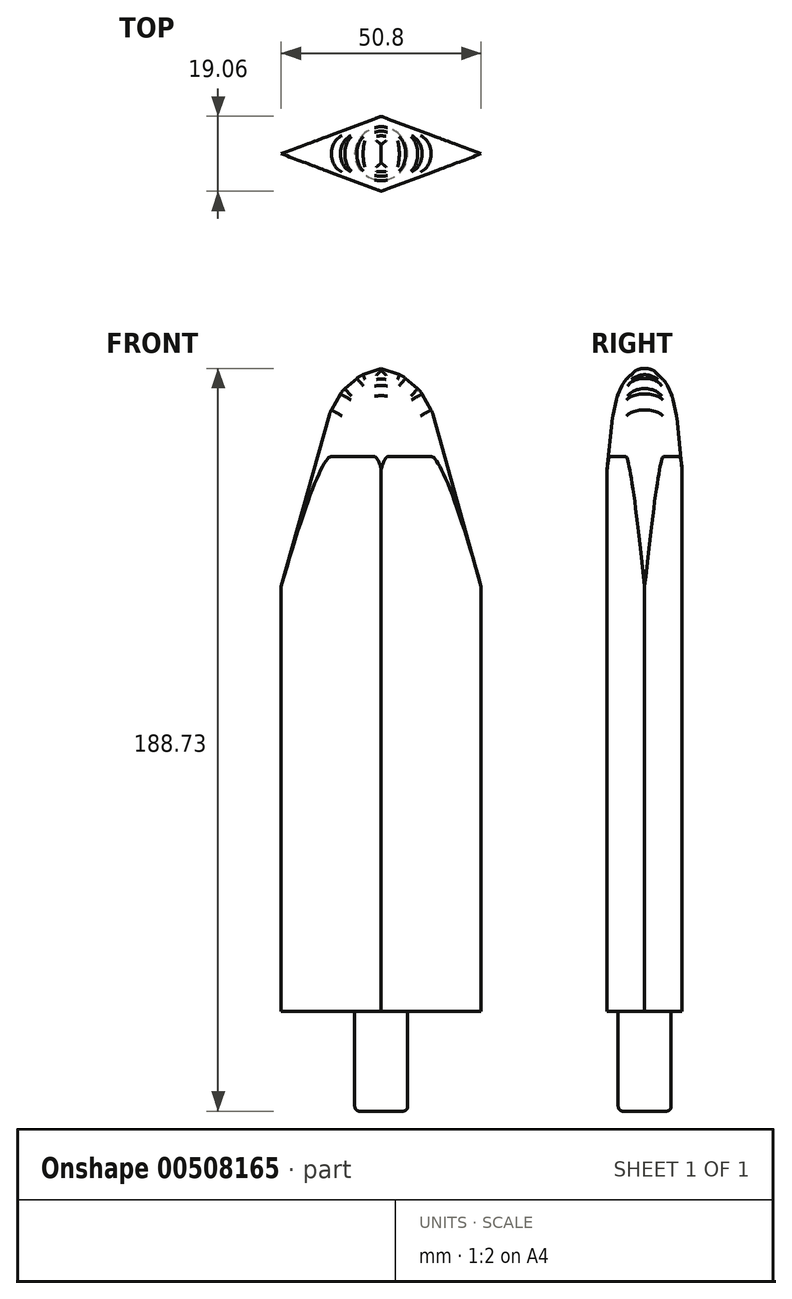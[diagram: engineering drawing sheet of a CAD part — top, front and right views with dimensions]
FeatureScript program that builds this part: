
annotation { "Feature Type Name" : "Feature", "Feature Type Description" : "" }
export const myFeature = defineFeature(function(context is Context, id is Id, definition is map)
    precondition{}
    {
        {
            var Q0;
            Q0=qCreatedBy(makeId("Top.planeOp"),FACE);
            var sketch = newSketch(context, id + "F0", { "sketchPlane" : qUnion([Q0])});
            skLineSegment(sketch, "E0", {"start": v(0, 0) * mm, "end": v(0, 9.53) * mm, "construction": true});
            skLineSegment(sketch, "E1", {"start": v(0, 9.53) * mm, "end": v(0, -9.52) * mm, "construction": true});
            skLineSegment(sketch, "E2", {"start": v(-25.4, 0) * mm, "end": v(25.4, 0) * mm, "construction": true});
            skLineSegment(sketch, "E3", {"start": v(0, 9.53) * mm, "end": v(-25.4, 0) * mm});
            skLineSegment(sketch, "E4", {"start": v(0, 9.53) * mm, "end": v(25.4, 0) * mm});
            skLineSegment(sketch, "E5", {"start": v(25.4, 0) * mm, "end": v(0, -9.52) * mm});
            skLineSegment(sketch, "E6", {"start": v(-25.4, 0) * mm, "end": v(0, -9.52) * mm});
            skSolve(sketch);
        }
        {
            var Q0;
            Q0=qSketchRegion(id+"F0",true);
            extrude(context, id + "F1", {"entities" : qUnion([Q0]), "depth" : 165.1 * mm});
        }
        {
            var Q0;
            Q0=qCreatedBy(makeId("Top.planeOp"),FACE);
            var sketch = newSketch(context, id + "F2", { "sketchPlane" : qUnion([Q0])});
            skCircle(sketch, "E7", {"center": v(0, 0) * mm, "radius": 6.73 * mm});
            skSolve(sketch);
        }
        {
            var Q0;
            Q0=qSketchRegion(id+"F2",true);
            extrude(context, id + "F3", {"entities" : qUnion([Q0]), "operationType" : NewBodyOperationType.ADD, "oppositeDirection" : true, "depth" : 25.4 * mm});
        }
        {
            var Q0;
            Q0=makeQuery(id+"F1.opExtrude","CAP_EDGE",EDGE,{"disambiguationData":[OSD([sQuery(id+"F0.wireOp",EDGE,"E5")])],"isStart":false});
            var Q1;
            Q1=makeQuery(id+"F1.opExtrude","CAP_EDGE",EDGE,{"disambiguationData":[OSD([sQuery(id+"F0.wireOp",EDGE,"E6")])],"isStart":false});
            var Q2;
            Q2=makeQuery(id+"F1.opExtrude","CAP_EDGE",EDGE,{"disambiguationData":[OSD([sQuery(id+"F0.wireOp",EDGE,"E3")])],"isStart":false});
            var Q3;
            Q3=makeQuery(id+"F1.opExtrude","CAP_EDGE",EDGE,{"disambiguationData":[OSD([sQuery(id+"F0.wireOp",EDGE,"E4")])],"isStart":false});
            chamfer(context, id + "F4", {"entities" : qUnion([Q0, Q1, Q2, Q3]), "width" : 8.9 * mm, "tangentPropagation" : true});
        }
        {
            var Q0;
            {var subQ0=sQuery(id+"F0.wireOp",EDGE,"E5");Q0=makeQuery(id+"F4.opChamfer","BLEND_EDGE",EDGE,{"blendedFrom":[makeQuery(id+"F1.opExtrude","CAP_EDGE",EDGE,{"disambiguationData":[OSD([subQ0])],"isStart":false}),makeQuery(id+"F1.opExtrude","SWEPT_FACE",FACE,{"disambiguationData":[OSD([subQ0])]})],"blendedInto":[makeQuery(id+"F1.opExtrude","SWEPT_FACE",FACE,{"disambiguationData":[OSD([subQ0])]})]});}
            var Q1;
            {var subQ0=sQuery(id+"F0.wireOp",EDGE,"E6");Q1=makeQuery(id+"F4.opChamfer","BLEND_EDGE",EDGE,{"blendedFrom":[makeQuery(id+"F1.opExtrude","CAP_EDGE",EDGE,{"disambiguationData":[OSD([subQ0])],"isStart":false}),makeQuery(id+"F1.opExtrude","SWEPT_FACE",FACE,{"disambiguationData":[OSD([subQ0])]})],"blendedInto":[makeQuery(id+"F1.opExtrude","SWEPT_FACE",FACE,{"disambiguationData":[OSD([subQ0])]})]});}
            var Q2;
            {var subQ0=sQuery(id+"F0.wireOp",EDGE,"E4");Q2=makeQuery(id+"F4.opChamfer","BLEND_EDGE",EDGE,{"blendedFrom":[makeQuery(id+"F1.opExtrude","CAP_EDGE",EDGE,{"disambiguationData":[OSD([subQ0])],"isStart":false}),makeQuery(id+"F1.opExtrude","SWEPT_FACE",FACE,{"disambiguationData":[OSD([subQ0])]})],"blendedInto":[makeQuery(id+"F1.opExtrude","SWEPT_FACE",FACE,{"disambiguationData":[OSD([subQ0])]})]});}
            var Q3;
            {var subQ0=sQuery(id+"F0.wireOp",EDGE,"E3");Q3=makeQuery(id+"F4.opChamfer","BLEND_EDGE",EDGE,{"blendedFrom":[makeQuery(id+"F1.opExtrude","CAP_EDGE",EDGE,{"disambiguationData":[OSD([subQ0])],"isStart":false}),makeQuery(id+"F1.opExtrude","SWEPT_FACE",FACE,{"disambiguationData":[OSD([subQ0])]})],"blendedInto":[makeQuery(id+"F1.opExtrude","SWEPT_FACE",FACE,{"disambiguationData":[OSD([subQ0])]})]});}
            chamfer(context, id + "F5", {"entities" : qUnion([Q0, Q1, Q2, Q3]), "width" : 5.08 * mm, "tangentPropagation" : true});
        }
        {
            var Q0;
            {var subQ0=sQuery(id+"F0.wireOp",EDGE,"E4");var subQ1=makeQuery(id+"F1.opExtrude","SWEPT_FACE",FACE,{"disambiguationData":[OSD([subQ0])]});Q0=makeQuery(id+"F5.opChamfer","BLEND_EDGE",EDGE,{"blendedFrom":[makeQuery(id+"F4.opChamfer","BLEND_EDGE",EDGE,{"blendedFrom":[makeQuery(id+"F1.opExtrude","CAP_EDGE",EDGE,{"disambiguationData":[OSD([subQ0])],"isStart":false}),subQ1],"blendedInto":[subQ1]}),subQ1],"blendedInto":[subQ1]});}
            var Q1;
            {var subQ0=sQuery(id+"F0.wireOp",EDGE,"E3");var subQ1=makeQuery(id+"F1.opExtrude","SWEPT_FACE",FACE,{"disambiguationData":[OSD([subQ0])]});Q1=makeQuery(id+"F5.opChamfer","BLEND_EDGE",EDGE,{"blendedFrom":[makeQuery(id+"F4.opChamfer","BLEND_EDGE",EDGE,{"blendedFrom":[makeQuery(id+"F1.opExtrude","CAP_EDGE",EDGE,{"disambiguationData":[OSD([subQ0])],"isStart":false}),subQ1],"blendedInto":[subQ1]}),subQ1],"blendedInto":[subQ1]});}
            var Q2;
            {var subQ0=sQuery(id+"F0.wireOp",EDGE,"E6");var subQ1=makeQuery(id+"F1.opExtrude","SWEPT_FACE",FACE,{"disambiguationData":[OSD([subQ0])]});Q2=makeQuery(id+"F5.opChamfer","BLEND_EDGE",EDGE,{"blendedFrom":[makeQuery(id+"F4.opChamfer","BLEND_EDGE",EDGE,{"blendedFrom":[makeQuery(id+"F1.opExtrude","CAP_EDGE",EDGE,{"disambiguationData":[OSD([subQ0])],"isStart":false}),subQ1],"blendedInto":[subQ1]}),subQ1],"blendedInto":[subQ1]});}
            var Q3;
            {var subQ0=sQuery(id+"F0.wireOp",EDGE,"E5");var subQ1=makeQuery(id+"F1.opExtrude","SWEPT_FACE",FACE,{"disambiguationData":[OSD([subQ0])]});Q3=makeQuery(id+"F5.opChamfer","BLEND_EDGE",EDGE,{"blendedFrom":[makeQuery(id+"F4.opChamfer","BLEND_EDGE",EDGE,{"blendedFrom":[makeQuery(id+"F1.opExtrude","CAP_EDGE",EDGE,{"disambiguationData":[OSD([subQ0])],"isStart":false}),subQ1],"blendedInto":[subQ1]}),subQ1],"blendedInto":[subQ1]});}
            chamfer(context, id + "F6", {"entities" : qUnion([Q0, Q1, Q2, Q3]), "width" : 5.08 * mm, "tangentPropagation" : true});
        }
        {
            var Q0;
            {var subQ0=sQuery(id+"F0.wireOp",EDGE,"E4");var subQ1=makeQuery(id+"F1.opExtrude","SWEPT_FACE",FACE,{"disambiguationData":[OSD([subQ0])]});var subQ2=subQ1;Q0=makeQuery(id+"F6.opChamfer","BLEND_EDGE",EDGE,{"blendedFrom":[makeQuery(id+"F5.opChamfer","BLEND_EDGE",EDGE,{"blendedFrom":[makeQuery(id+"F4.opChamfer","BLEND_EDGE",EDGE,{"blendedFrom":[makeQuery(id+"F1.opExtrude","CAP_EDGE",EDGE,{"disambiguationData":[OSD([subQ0])],"isStart":false}),subQ1],"blendedInto":[subQ1]}),subQ2],"blendedInto":[subQ2]}),subQ2],"blendedInto":[subQ2]});}
            var Q1;
            {var subQ0=sQuery(id+"F0.wireOp",EDGE,"E3");var subQ1=makeQuery(id+"F1.opExtrude","SWEPT_FACE",FACE,{"disambiguationData":[OSD([subQ0])]});var subQ2=subQ1;Q1=makeQuery(id+"F6.opChamfer","BLEND_EDGE",EDGE,{"blendedFrom":[makeQuery(id+"F5.opChamfer","BLEND_EDGE",EDGE,{"blendedFrom":[makeQuery(id+"F4.opChamfer","BLEND_EDGE",EDGE,{"blendedFrom":[makeQuery(id+"F1.opExtrude","CAP_EDGE",EDGE,{"disambiguationData":[OSD([subQ0])],"isStart":false}),subQ1],"blendedInto":[subQ1]}),subQ2],"blendedInto":[subQ2]}),subQ2],"blendedInto":[subQ2]});}
            var Q2;
            {var subQ0=sQuery(id+"F0.wireOp",EDGE,"E6");var subQ1=makeQuery(id+"F1.opExtrude","SWEPT_FACE",FACE,{"disambiguationData":[OSD([subQ0])]});var subQ2=subQ1;Q2=makeQuery(id+"F6.opChamfer","BLEND_EDGE",EDGE,{"blendedFrom":[makeQuery(id+"F5.opChamfer","BLEND_EDGE",EDGE,{"blendedFrom":[makeQuery(id+"F4.opChamfer","BLEND_EDGE",EDGE,{"blendedFrom":[makeQuery(id+"F1.opExtrude","CAP_EDGE",EDGE,{"disambiguationData":[OSD([subQ0])],"isStart":false}),subQ1],"blendedInto":[subQ1]}),subQ2],"blendedInto":[subQ2]}),subQ2],"blendedInto":[subQ2]});}
            var Q3;
            {var subQ0=sQuery(id+"F0.wireOp",EDGE,"E5");var subQ1=makeQuery(id+"F1.opExtrude","SWEPT_FACE",FACE,{"disambiguationData":[OSD([subQ0])]});var subQ2=subQ1;Q3=makeQuery(id+"F6.opChamfer","BLEND_EDGE",EDGE,{"blendedFrom":[makeQuery(id+"F5.opChamfer","BLEND_EDGE",EDGE,{"blendedFrom":[makeQuery(id+"F4.opChamfer","BLEND_EDGE",EDGE,{"blendedFrom":[makeQuery(id+"F1.opExtrude","CAP_EDGE",EDGE,{"disambiguationData":[OSD([subQ0])],"isStart":false}),subQ1],"blendedInto":[subQ1]}),subQ2],"blendedInto":[subQ2]}),subQ2],"blendedInto":[subQ2]});}
            chamfer(context, id + "F7", {"entities" : qUnion([Q0, Q1, Q2, Q3]), "width" : 5.08 * mm, "tangentPropagation" : true});
        }
        {
            var Q0;
            {var subQ0=sQuery(id+"F0.wireOp",EDGE,"E4");var subQ1=makeQuery(id+"F1.opExtrude","SWEPT_FACE",FACE,{"disambiguationData":[OSD([subQ0])]});var subQ2=subQ1;Q0=makeQuery(id+"F7.opChamfer","BLEND_EDGE",EDGE,{"blendedFrom":[makeQuery(id+"F6.opChamfer","BLEND_EDGE",EDGE,{"blendedFrom":[makeQuery(id+"F5.opChamfer","BLEND_EDGE",EDGE,{"blendedFrom":[makeQuery(id+"F4.opChamfer","BLEND_EDGE",EDGE,{"blendedFrom":[makeQuery(id+"F1.opExtrude","CAP_EDGE",EDGE,{"disambiguationData":[OSD([subQ0])],"isStart":false}),subQ1],"blendedInto":[subQ1]}),subQ2],"blendedInto":[subQ2]}),subQ2],"blendedInto":[subQ2]}),makeQuery(id+"F6.opChamfer","BLEND_FACE",FACE,{"disambiguationData":[OSD([subQ0])]})],"blendedInto":[makeQuery(id+"F6.opChamfer","BLEND_FACE",FACE,{"disambiguationData":[OSD([subQ0])]})]});}
            var Q1;
            {var subQ0=sQuery(id+"F0.wireOp",EDGE,"E4");var subQ1=makeQuery(id+"F1.opExtrude","SWEPT_FACE",FACE,{"disambiguationData":[OSD([subQ0])]});Q1=makeQuery(id+"F6.opChamfer","BLEND_EDGE",EDGE,{"blendedFrom":[makeQuery(id+"F5.opChamfer","BLEND_EDGE",EDGE,{"blendedFrom":[makeQuery(id+"F4.opChamfer","BLEND_EDGE",EDGE,{"blendedFrom":[makeQuery(id+"F1.opExtrude","CAP_EDGE",EDGE,{"disambiguationData":[OSD([subQ0])],"isStart":false}),subQ1],"blendedInto":[subQ1]}),subQ1],"blendedInto":[subQ1]}),makeQuery(id+"F5.opChamfer","BLEND_FACE",FACE,{"disambiguationData":[OSD([subQ0])]})],"blendedInto":[makeQuery(id+"F5.opChamfer","BLEND_FACE",FACE,{"disambiguationData":[OSD([subQ0])]})]});}
            var Q2;
            {var subQ0=sQuery(id+"F0.wireOp",EDGE,"E3");var subQ1=makeQuery(id+"F1.opExtrude","SWEPT_FACE",FACE,{"disambiguationData":[OSD([subQ0])]});var subQ2=subQ1;Q2=makeQuery(id+"F7.opChamfer","BLEND_EDGE",EDGE,{"blendedFrom":[makeQuery(id+"F6.opChamfer","BLEND_EDGE",EDGE,{"blendedFrom":[makeQuery(id+"F5.opChamfer","BLEND_EDGE",EDGE,{"blendedFrom":[makeQuery(id+"F4.opChamfer","BLEND_EDGE",EDGE,{"blendedFrom":[makeQuery(id+"F1.opExtrude","CAP_EDGE",EDGE,{"disambiguationData":[OSD([subQ0])],"isStart":false}),subQ1],"blendedInto":[subQ1]}),subQ2],"blendedInto":[subQ2]}),subQ2],"blendedInto":[subQ2]}),makeQuery(id+"F6.opChamfer","BLEND_FACE",FACE,{"disambiguationData":[OSD([subQ0])]})],"blendedInto":[makeQuery(id+"F6.opChamfer","BLEND_FACE",FACE,{"disambiguationData":[OSD([subQ0])]})]});}
            var Q3;
            {var subQ0=sQuery(id+"F0.wireOp",EDGE,"E3");var subQ1=makeQuery(id+"F1.opExtrude","SWEPT_FACE",FACE,{"disambiguationData":[OSD([subQ0])]});Q3=makeQuery(id+"F6.opChamfer","BLEND_EDGE",EDGE,{"blendedFrom":[makeQuery(id+"F5.opChamfer","BLEND_EDGE",EDGE,{"blendedFrom":[makeQuery(id+"F4.opChamfer","BLEND_EDGE",EDGE,{"blendedFrom":[makeQuery(id+"F1.opExtrude","CAP_EDGE",EDGE,{"disambiguationData":[OSD([subQ0])],"isStart":false}),subQ1],"blendedInto":[subQ1]}),subQ1],"blendedInto":[subQ1]}),makeQuery(id+"F5.opChamfer","BLEND_FACE",FACE,{"disambiguationData":[OSD([subQ0])]})],"blendedInto":[makeQuery(id+"F5.opChamfer","BLEND_FACE",FACE,{"disambiguationData":[OSD([subQ0])]})]});}
            var Q4;
            {var subQ0=sQuery(id+"F0.wireOp",EDGE,"E3");Q4=makeQuery(id+"F5.opChamfer","BLEND_EDGE",EDGE,{"blendedFrom":[makeQuery(id+"F4.opChamfer","BLEND_EDGE",EDGE,{"blendedFrom":[makeQuery(id+"F1.opExtrude","CAP_EDGE",EDGE,{"disambiguationData":[OSD([subQ0])],"isStart":false}),makeQuery(id+"F1.opExtrude","SWEPT_FACE",FACE,{"disambiguationData":[OSD([subQ0])]})],"blendedInto":[makeQuery(id+"F1.opExtrude","SWEPT_FACE",FACE,{"disambiguationData":[OSD([subQ0])]})]}),makeQuery(id+"F4.opChamfer","BLEND_FACE",FACE,{"disambiguationData":[OSD([subQ0])]})],"blendedInto":[makeQuery(id+"F4.opChamfer","BLEND_FACE",FACE,{"disambiguationData":[OSD([subQ0])]})]});}
            var Q5;
            {var subQ0=sQuery(id+"F0.wireOp",EDGE,"E4");Q5=makeQuery(id+"F5.opChamfer","BLEND_EDGE",EDGE,{"blendedFrom":[makeQuery(id+"F4.opChamfer","BLEND_EDGE",EDGE,{"blendedFrom":[makeQuery(id+"F1.opExtrude","CAP_EDGE",EDGE,{"disambiguationData":[OSD([subQ0])],"isStart":false}),makeQuery(id+"F1.opExtrude","SWEPT_FACE",FACE,{"disambiguationData":[OSD([subQ0])]})],"blendedInto":[makeQuery(id+"F1.opExtrude","SWEPT_FACE",FACE,{"disambiguationData":[OSD([subQ0])]})]}),makeQuery(id+"F4.opChamfer","BLEND_FACE",FACE,{"disambiguationData":[OSD([subQ0])]})],"blendedInto":[makeQuery(id+"F4.opChamfer","BLEND_FACE",FACE,{"disambiguationData":[OSD([subQ0])]})]});}
            var Q6;
            {var subQ0=sQuery(id+"F0.wireOp",EDGE,"E5");var subQ1=makeQuery(id+"F1.opExtrude","SWEPT_FACE",FACE,{"disambiguationData":[OSD([subQ0])]});var subQ2=subQ1;Q6=makeQuery(id+"F7.opChamfer","BLEND_EDGE",EDGE,{"blendedFrom":[makeQuery(id+"F6.opChamfer","BLEND_EDGE",EDGE,{"blendedFrom":[makeQuery(id+"F5.opChamfer","BLEND_EDGE",EDGE,{"blendedFrom":[makeQuery(id+"F4.opChamfer","BLEND_EDGE",EDGE,{"blendedFrom":[makeQuery(id+"F1.opExtrude","CAP_EDGE",EDGE,{"disambiguationData":[OSD([subQ0])],"isStart":false}),subQ1],"blendedInto":[subQ1]}),subQ2],"blendedInto":[subQ2]}),subQ2],"blendedInto":[subQ2]}),makeQuery(id+"F6.opChamfer","BLEND_FACE",FACE,{"disambiguationData":[OSD([subQ0])]})],"blendedInto":[makeQuery(id+"F6.opChamfer","BLEND_FACE",FACE,{"disambiguationData":[OSD([subQ0])]})]});}
            var Q7;
            {var subQ0=sQuery(id+"F0.wireOp",EDGE,"E6");var subQ1=makeQuery(id+"F1.opExtrude","SWEPT_FACE",FACE,{"disambiguationData":[OSD([subQ0])]});Q7=makeQuery(id+"F6.opChamfer","BLEND_EDGE",EDGE,{"blendedFrom":[makeQuery(id+"F5.opChamfer","BLEND_EDGE",EDGE,{"blendedFrom":[makeQuery(id+"F4.opChamfer","BLEND_EDGE",EDGE,{"blendedFrom":[makeQuery(id+"F1.opExtrude","CAP_EDGE",EDGE,{"disambiguationData":[OSD([subQ0])],"isStart":false}),subQ1],"blendedInto":[subQ1]}),subQ1],"blendedInto":[subQ1]}),makeQuery(id+"F5.opChamfer","BLEND_FACE",FACE,{"disambiguationData":[OSD([subQ0])]})],"blendedInto":[makeQuery(id+"F5.opChamfer","BLEND_FACE",FACE,{"disambiguationData":[OSD([subQ0])]})]});}
            var Q8;
            {var subQ0=sQuery(id+"F0.wireOp",EDGE,"E6");var subQ1=makeQuery(id+"F1.opExtrude","SWEPT_FACE",FACE,{"disambiguationData":[OSD([subQ0])]});var subQ2=subQ1;Q8=makeQuery(id+"F7.opChamfer","BLEND_EDGE",EDGE,{"blendedFrom":[makeQuery(id+"F6.opChamfer","BLEND_EDGE",EDGE,{"blendedFrom":[makeQuery(id+"F5.opChamfer","BLEND_EDGE",EDGE,{"blendedFrom":[makeQuery(id+"F4.opChamfer","BLEND_EDGE",EDGE,{"blendedFrom":[makeQuery(id+"F1.opExtrude","CAP_EDGE",EDGE,{"disambiguationData":[OSD([subQ0])],"isStart":false}),subQ1],"blendedInto":[subQ1]}),subQ2],"blendedInto":[subQ2]}),subQ2],"blendedInto":[subQ2]}),makeQuery(id+"F6.opChamfer","BLEND_FACE",FACE,{"disambiguationData":[OSD([subQ0])]})],"blendedInto":[makeQuery(id+"F6.opChamfer","BLEND_FACE",FACE,{"disambiguationData":[OSD([subQ0])]})]});}
            var Q9;
            {var subQ0=sQuery(id+"F0.wireOp",EDGE,"E5");var subQ1=makeQuery(id+"F1.opExtrude","SWEPT_FACE",FACE,{"disambiguationData":[OSD([subQ0])]});Q9=makeQuery(id+"F6.opChamfer","BLEND_EDGE",EDGE,{"blendedFrom":[makeQuery(id+"F5.opChamfer","BLEND_EDGE",EDGE,{"blendedFrom":[makeQuery(id+"F4.opChamfer","BLEND_EDGE",EDGE,{"blendedFrom":[makeQuery(id+"F1.opExtrude","CAP_EDGE",EDGE,{"disambiguationData":[OSD([subQ0])],"isStart":false}),subQ1],"blendedInto":[subQ1]}),subQ1],"blendedInto":[subQ1]}),makeQuery(id+"F5.opChamfer","BLEND_FACE",FACE,{"disambiguationData":[OSD([subQ0])]})],"blendedInto":[makeQuery(id+"F5.opChamfer","BLEND_FACE",FACE,{"disambiguationData":[OSD([subQ0])]})]});}
            var Q10;
            {var subQ0=sQuery(id+"F0.wireOp",EDGE,"E5");Q10=makeQuery(id+"F5.opChamfer","BLEND_EDGE",EDGE,{"blendedFrom":[makeQuery(id+"F4.opChamfer","BLEND_EDGE",EDGE,{"blendedFrom":[makeQuery(id+"F1.opExtrude","CAP_EDGE",EDGE,{"disambiguationData":[OSD([subQ0])],"isStart":false}),makeQuery(id+"F1.opExtrude","SWEPT_FACE",FACE,{"disambiguationData":[OSD([subQ0])]})],"blendedInto":[makeQuery(id+"F1.opExtrude","SWEPT_FACE",FACE,{"disambiguationData":[OSD([subQ0])]})]}),makeQuery(id+"F4.opChamfer","BLEND_FACE",FACE,{"disambiguationData":[OSD([subQ0])]})],"blendedInto":[makeQuery(id+"F4.opChamfer","BLEND_FACE",FACE,{"disambiguationData":[OSD([subQ0])]})]});}
            var Q11;
            {var subQ0=sQuery(id+"F0.wireOp",EDGE,"E6");Q11=makeQuery(id+"F5.opChamfer","BLEND_EDGE",EDGE,{"blendedFrom":[makeQuery(id+"F4.opChamfer","BLEND_EDGE",EDGE,{"blendedFrom":[makeQuery(id+"F1.opExtrude","CAP_EDGE",EDGE,{"disambiguationData":[OSD([subQ0])],"isStart":false}),makeQuery(id+"F1.opExtrude","SWEPT_FACE",FACE,{"disambiguationData":[OSD([subQ0])]})],"blendedInto":[makeQuery(id+"F1.opExtrude","SWEPT_FACE",FACE,{"disambiguationData":[OSD([subQ0])]})]}),makeQuery(id+"F4.opChamfer","BLEND_FACE",FACE,{"disambiguationData":[OSD([subQ0])]})],"blendedInto":[makeQuery(id+"F4.opChamfer","BLEND_FACE",FACE,{"disambiguationData":[OSD([subQ0])]})]});}
            fillet(context, id + "F8", {"entities" : qUnion([Q0, Q1, Q2, Q3, Q4, Q5, Q6, Q7, Q8, Q9, Q10, Q11]), "radius" : 5.08 * mm, "tangentPropagation" : true, "allowEdgeOverflow" : false});
        }
        {
            var Q0;
            {var subQ0=sQuery(id+"F0.wireOp",EDGE,"E6");var subQ1=makeQuery(id+"F1.opExtrude","SWEPT_FACE",FACE,{"disambiguationData":[OSD([subQ0])]});var subQ2=subQ1;var subQ3=sQuery(id+"F0.wireOp",EDGE,"E3");var subQ4=makeQuery(id+"F1.opExtrude","SWEPT_FACE",FACE,{"disambiguationData":[OSD([subQ3])]});var subQ5=subQ4;Q0=makeQuery(id+"F7.opChamfer","BLEND_EDGE",EDGE,{"blendedFrom":[makeQuery(id+"F6.opChamfer","BLEND_EDGE",EDGE,{"blendedFrom":[makeQuery(id+"F5.opChamfer","BLEND_EDGE",EDGE,{"blendedFrom":[makeQuery(id+"F4.opChamfer","BLEND_EDGE",EDGE,{"blendedFrom":[makeQuery(id+"F1.opExtrude","CAP_EDGE",EDGE,{"disambiguationData":[OSD([subQ3])],"isStart":false}),subQ4],"blendedInto":[subQ4]}),subQ5],"blendedInto":[subQ5]}),subQ5],"blendedInto":[subQ5]}),makeQuery(id+"F6.opChamfer","BLEND_EDGE",EDGE,{"blendedFrom":[makeQuery(id+"F5.opChamfer","BLEND_EDGE",EDGE,{"blendedFrom":[makeQuery(id+"F4.opChamfer","BLEND_EDGE",EDGE,{"blendedFrom":[makeQuery(id+"F1.opExtrude","CAP_EDGE",EDGE,{"disambiguationData":[OSD([subQ0])],"isStart":false}),subQ1],"blendedInto":[subQ1]}),subQ2],"blendedInto":[subQ2]}),subQ2],"blendedInto":[subQ2]})],"blendedInto":[]});}
            var Q1;
            {var subQ0=sQuery(id+"F0.wireOp",EDGE,"E4");var subQ1=makeQuery(id+"F1.opExtrude","SWEPT_FACE",FACE,{"disambiguationData":[OSD([subQ0])]});var subQ2=subQ1;var subQ3=sQuery(id+"F0.wireOp",EDGE,"E3");var subQ4=makeQuery(id+"F1.opExtrude","SWEPT_FACE",FACE,{"disambiguationData":[OSD([subQ3])]});var subQ5=subQ4;Q1=makeQuery(id+"F7.opChamfer","BLEND_EDGE",EDGE,{"blendedFrom":[makeQuery(id+"F6.opChamfer","BLEND_EDGE",EDGE,{"blendedFrom":[makeQuery(id+"F5.opChamfer","BLEND_EDGE",EDGE,{"blendedFrom":[makeQuery(id+"F4.opChamfer","BLEND_EDGE",EDGE,{"blendedFrom":[makeQuery(id+"F1.opExtrude","CAP_EDGE",EDGE,{"disambiguationData":[OSD([subQ3])],"isStart":false}),subQ4],"blendedInto":[subQ4]}),subQ5],"blendedInto":[subQ5]}),subQ5],"blendedInto":[subQ5]}),makeQuery(id+"F6.opChamfer","BLEND_EDGE",EDGE,{"blendedFrom":[makeQuery(id+"F5.opChamfer","BLEND_EDGE",EDGE,{"blendedFrom":[makeQuery(id+"F4.opChamfer","BLEND_EDGE",EDGE,{"blendedFrom":[makeQuery(id+"F1.opExtrude","CAP_EDGE",EDGE,{"disambiguationData":[OSD([subQ0])],"isStart":false}),subQ1],"blendedInto":[subQ1]}),subQ2],"blendedInto":[subQ2]}),subQ2],"blendedInto":[subQ2]})],"blendedInto":[]});}
            var Q2;
            {var subQ0=sQuery(id+"F0.wireOp",EDGE,"E6");var subQ1=makeQuery(id+"F1.opExtrude","SWEPT_FACE",FACE,{"disambiguationData":[OSD([subQ0])]});var subQ2=subQ1;var subQ3=sQuery(id+"F0.wireOp",EDGE,"E5");var subQ4=makeQuery(id+"F1.opExtrude","SWEPT_FACE",FACE,{"disambiguationData":[OSD([subQ3])]});var subQ5=subQ4;Q2=makeQuery(id+"F7.opChamfer","BLEND_EDGE",EDGE,{"blendedFrom":[makeQuery(id+"F6.opChamfer","BLEND_EDGE",EDGE,{"blendedFrom":[makeQuery(id+"F5.opChamfer","BLEND_EDGE",EDGE,{"blendedFrom":[makeQuery(id+"F4.opChamfer","BLEND_EDGE",EDGE,{"blendedFrom":[makeQuery(id+"F1.opExtrude","CAP_EDGE",EDGE,{"disambiguationData":[OSD([subQ3])],"isStart":false}),subQ4],"blendedInto":[subQ4]}),subQ5],"blendedInto":[subQ5]}),subQ5],"blendedInto":[subQ5]}),makeQuery(id+"F6.opChamfer","BLEND_EDGE",EDGE,{"blendedFrom":[makeQuery(id+"F5.opChamfer","BLEND_EDGE",EDGE,{"blendedFrom":[makeQuery(id+"F4.opChamfer","BLEND_EDGE",EDGE,{"blendedFrom":[makeQuery(id+"F1.opExtrude","CAP_EDGE",EDGE,{"disambiguationData":[OSD([subQ0])],"isStart":false}),subQ1],"blendedInto":[subQ1]}),subQ2],"blendedInto":[subQ2]}),subQ2],"blendedInto":[subQ2]})],"blendedInto":[]});}
            var Q3;
            {var subQ0=sQuery(id+"F0.wireOp",EDGE,"E5");var subQ1=makeQuery(id+"F1.opExtrude","SWEPT_FACE",FACE,{"disambiguationData":[OSD([subQ0])]});var subQ2=subQ1;var subQ3=sQuery(id+"F0.wireOp",EDGE,"E4");var subQ4=makeQuery(id+"F1.opExtrude","SWEPT_FACE",FACE,{"disambiguationData":[OSD([subQ3])]});var subQ5=subQ4;Q3=makeQuery(id+"F7.opChamfer","BLEND_EDGE",EDGE,{"blendedFrom":[makeQuery(id+"F6.opChamfer","BLEND_EDGE",EDGE,{"blendedFrom":[makeQuery(id+"F5.opChamfer","BLEND_EDGE",EDGE,{"blendedFrom":[makeQuery(id+"F4.opChamfer","BLEND_EDGE",EDGE,{"blendedFrom":[makeQuery(id+"F1.opExtrude","CAP_EDGE",EDGE,{"disambiguationData":[OSD([subQ3])],"isStart":false}),subQ4],"blendedInto":[subQ4]}),subQ5],"blendedInto":[subQ5]}),subQ5],"blendedInto":[subQ5]}),makeQuery(id+"F6.opChamfer","BLEND_EDGE",EDGE,{"blendedFrom":[makeQuery(id+"F5.opChamfer","BLEND_EDGE",EDGE,{"blendedFrom":[makeQuery(id+"F4.opChamfer","BLEND_EDGE",EDGE,{"blendedFrom":[makeQuery(id+"F1.opExtrude","CAP_EDGE",EDGE,{"disambiguationData":[OSD([subQ0])],"isStart":false}),subQ1],"blendedInto":[subQ1]}),subQ2],"blendedInto":[subQ2]}),subQ2],"blendedInto":[subQ2]})],"blendedInto":[]});}
            fillet(context, id + "F9", {"entities" : qUnion([Q0, Q1, Q2, Q3]), "radius" : 5.08 * mm, "tangentPropagation" : true, "allowEdgeOverflow" : false});
        }
        {
            var Q0;
            Q0=makeQuery(id+"F3.opExtrude","CAP_EDGE",EDGE,{"disambiguationData":[OSD([sQuery(id+"F2.wireOp",EDGE,"E7")])],"isStart":true});
            var Q1;
            Q1=makeQuery(id+"F3.opExtrude","CAP_EDGE",EDGE,{"disambiguationData":[OSD([sQuery(id+"F2.wireOp",EDGE,"E7")])],"isStart":false});
            fillet(context, id + "F10", {"entities" : qUnion([Q0, Q1]), "radius" : 1.27 * mm, "tangentPropagation" : true, "allowEdgeOverflow" : false});
        }
    });
